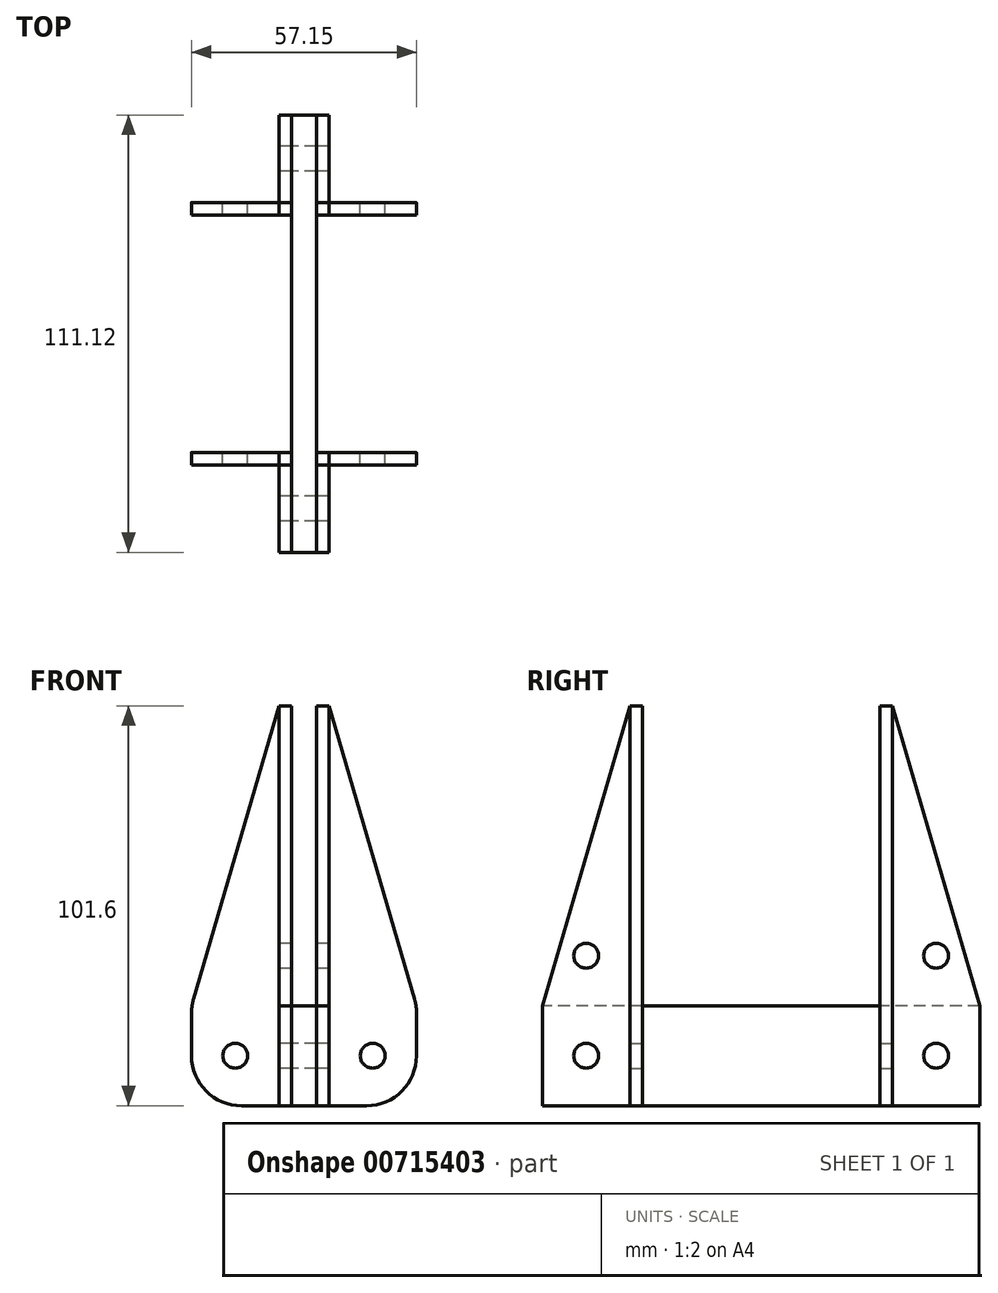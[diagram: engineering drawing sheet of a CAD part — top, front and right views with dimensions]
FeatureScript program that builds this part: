
annotation { "Feature Type Name" : "Feature", "Feature Type Description" : "" }
export const myFeature = defineFeature(function(context is Context, id is Id, definition is map)
    precondition{}
    {
        {
            var Q0;
            Q0=qCreatedBy(makeId("Top.planeOp"),FACE);
            var sketch = newSketch(context, id + "F0", { "sketchPlane" : qUnion([Q0])});
            skLineSegment(sketch, "E0.bottom", {"start": v(-15.88, 101.6) * mm, "end": v(15.87, 101.6) * mm, "construction": true});
            skLineSegment(sketch, "E0.top", {"start": v(-15.87, -101.6) * mm, "end": v(15.87, -101.6) * mm, "construction": true});
            skLineSegment(sketch, "E0.left", {"start": v(-15.88, 101.6) * mm, "end": v(-15.87, -101.6) * mm, "construction": true});
            skLineSegment(sketch, "E0.right", {"start": v(15.87, 101.6) * mm, "end": v(15.88, -101.6) * mm, "construction": true});
            skLineSegment(sketch, "E1", {"start": v(-28.57, 30.16) * mm, "end": v(-3.17, 30.16) * mm});
            skLineSegment(sketch, "E2", {"start": v(-3.17, 30.16) * mm, "end": v(-3.18, 55.56) * mm});
            skLineSegment(sketch, "E3", {"start": v(15.88, 0) * mm, "end": v(-15.87, 0) * mm, "construction": true});
            skLineSegment(sketch, "E4", {"start": v(0, 101.6) * mm, "end": v(0, -101.6) * mm, "construction": true});
            skLineSegment(sketch, "E5.0", {"start": v(-6.35, 33.34) * mm, "end": v(-6.35, 55.56) * mm});
            skLineSegment(sketch, "E5.1", {"start": v(-28.57, 33.34) * mm, "end": v(-6.35, 33.34) * mm});
            skLineSegment(sketch, "E6", {"start": v(-28.57, 33.34) * mm, "end": v(-28.57, 30.16) * mm});
            skLineSegment(sketch, "E7", {"start": v(-3.18, 55.56) * mm, "end": v(-6.35, 55.56) * mm});
            skLineSegment(sketch, "E8.MirrorCS", {"start": v(3.17, 30.16) * mm, "end": v(3.17, 55.56) * mm});
            skLineSegment(sketch, "E9.MirrorCS", {"start": v(3.17, 55.56) * mm, "end": v(6.35, 55.56) * mm});
            skLineSegment(sketch, "E10.MirrorCS", {"start": v(6.35, 33.34) * mm, "end": v(6.35, 55.56) * mm});
            skLineSegment(sketch, "E11.MirrorCS", {"start": v(28.57, 33.34) * mm, "end": v(6.35, 33.34) * mm});
            skLineSegment(sketch, "E12.MirrorCS", {"start": v(28.57, 30.16) * mm, "end": v(3.17, 30.16) * mm});
            skLineSegment(sketch, "E13.MirrorCS", {"start": v(28.58, 33.34) * mm, "end": v(28.58, 30.16) * mm});
            skLineSegment(sketch, "E14.MirrorCS", {"start": v(3.17, -55.56) * mm, "end": v(6.35, -55.56) * mm});
            skLineSegment(sketch, "E15.MirrorCS", {"start": v(-3.17, -55.56) * mm, "end": v(-6.35, -55.56) * mm});
            skLineSegment(sketch, "E16.MirrorCS", {"start": v(28.58, -33.34) * mm, "end": v(28.58, -30.16) * mm});
            skLineSegment(sketch, "E17.MirrorCS", {"start": v(-28.57, -33.34) * mm, "end": v(-28.57, -30.16) * mm});
            skLineSegment(sketch, "E18.MirrorCS", {"start": v(28.57, -33.34) * mm, "end": v(6.35, -33.34) * mm});
            skLineSegment(sketch, "E19.MirrorCS", {"start": v(28.58, -30.16) * mm, "end": v(3.17, -30.16) * mm});
            skLineSegment(sketch, "E20.MirrorCS", {"start": v(6.35, -33.34) * mm, "end": v(6.35, -55.56) * mm});
            skLineSegment(sketch, "E21.MirrorCS", {"start": v(-28.57, -30.16) * mm, "end": v(-3.17, -30.16) * mm});
            skLineSegment(sketch, "E22.MirrorCS", {"start": v(3.18, -30.16) * mm, "end": v(3.18, -55.56) * mm});
            skLineSegment(sketch, "E23.MirrorCS", {"start": v(-3.17, -30.16) * mm, "end": v(-3.17, -55.56) * mm});
            skLineSegment(sketch, "E24.MirrorCS", {"start": v(-28.57, -33.34) * mm, "end": v(-6.35, -33.34) * mm});
            skLineSegment(sketch, "E25.MirrorCS", {"start": v(-6.35, -33.34) * mm, "end": v(-6.35, -55.56) * mm});
            skLineSegment(sketch, "E26", {"start": v(-3.17, -55.56) * mm, "end": v(3.17, -55.56) * mm});
            skLineSegment(sketch, "E27", {"start": v(-3.18, 55.56) * mm, "end": v(3.17, 55.56) * mm});
            skLineSegment(sketch, "E28", {"start": v(-3.17, -30.16) * mm, "end": v(-3.18, 30.16) * mm});
            skLineSegment(sketch, "E29", {"start": v(3.17, 30.16) * mm, "end": v(3.18, -30.16) * mm});
            skSolve(sketch);
        }
        {
            var Q0;
            Q0=makeQuery(id+"F0.imprint","IMPRINT",FACE,{"disambiguationData":[TD([[makeQuery(id+"F0.imprint","IMPRINT",EDGE,{"derivedFrom":sQuery(id+"F0.wireOp",EDGE,"E1")}),1.0]])]});
            var Q1;
            Q1=makeQuery(id+"F0.imprint","IMPRINT",FACE,{"disambiguationData":[TD([[makeQuery(id+"F0.imprint","IMPRINT",EDGE,{"derivedFrom":sQuery(id+"F0.wireOp",EDGE,"E8.MirrorCS")}),-1.0]])]});
            var Q2;
            Q2=makeQuery(id+"F0.imprint","IMPRINT",FACE,{"disambiguationData":[TD([[makeQuery(id+"F0.imprint","IMPRINT",EDGE,{"derivedFrom":sQuery(id+"F0.wireOp",EDGE,"E14.MirrorCS")}),1.0]])]});
            var Q3;
            Q3=makeQuery(id+"F0.imprint","IMPRINT",FACE,{"disambiguationData":[TD([[makeQuery(id+"F0.imprint","IMPRINT",EDGE,{"derivedFrom":sQuery(id+"F0.wireOp",EDGE,"E15.MirrorCS")}),-1.0]])]});
            extrude(context, id + "F1", {"entities" : qUnion([Q0, Q1, Q2, Q3]), "depth" : 101.6 * mm, "offsetDistance" : 25.4 * mm});
        }
        {
            var Q0;
            Q0=qCreatedBy(makeId("Front.planeOp"),FACE);
            var sketch = newSketch(context, id + "F2", { "sketchPlane" : qUnion([Q0])});
            skLineSegment(sketch, "E30", {"start": v(28.07, 27.14) * mm, "end": v(6.35, 101.6) * mm});
            skLineSegment(sketch, "E31", {"start": v(6.35, 101.6) * mm, "end": v(-6.35, 101.6) * mm});
            skLineSegment(sketch, "E32", {"start": v(-6.35, 101.6) * mm, "end": v(-28.07, 27.14) * mm});
            skLineSegment(sketch, "E33", {"start": v(-28.57, 23.59) * mm, "end": v(-28.57, 12.7) * mm});
            skLineSegment(sketch, "E34", {"start": v(28.58, 23.59) * mm, "end": v(28.58, 12.7) * mm});
            skLineSegment(sketch, "E35", {"start": v(15.88, 0) * mm, "end": v(-15.87, 0) * mm});
            skCircle(sketch, "E36", {"center": v(-17.46, 12.7) * mm, "radius": 3.18 * mm});
            skPoint(sketch, "E36.centerSnap0", {"position": v(-28.57, 12.7) * mm});
            skCircle(sketch, "E37.MirrorC", {"center": v(17.46, 12.7) * mm, "radius": 3.18 * mm});
            skPoint(sketch, "E38.visualSharp", {"position": v(28.58, 0) * mm});
            skArc(sketch, "E38.filletArc", {"start": v(15.88, 0) * mm, "mid": v(24.86, 3.72) * mm, "end": v(28.58, 12.7) * mm});
            skPoint(sketch, "E39.visualSharp", {"position": v(28.58, 25.4) * mm});
            skArc(sketch, "E39.filletArc", {"start": v(28.58, 23.59) * mm, "mid": v(28.45, 25.38) * mm, "end": v(28.07, 27.14) * mm});
            skPoint(sketch, "E40.visualSharp", {"position": v(-28.57, 0) * mm});
            skArc(sketch, "E40.filletArc", {"start": v(-28.57, 12.7) * mm, "mid": v(-24.86, 3.72) * mm, "end": v(-15.87, 0) * mm});
            skPoint(sketch, "E41.visualSharp", {"position": v(-28.57, 25.4) * mm});
            skArc(sketch, "E41.filletArc", {"start": v(-28.07, 27.14) * mm, "mid": v(-28.45, 25.38) * mm, "end": v(-28.58, 23.59) * mm});
            skSolve(sketch);
        }
        {
            var Q0;
            Q0 = qSketchRegion(id + "F2", true);
            extrude(context, id + "F3", {"entities" : qUnion([Q0]), "operationType" : NewBodyOperationType.INTERSECT, "endBound" : BoundingType.SYMMETRIC, "depth" : 203.2 * mm, "offsetDistance" : 25.4 * mm});
        }
        {
            var Q0;
            Q0=makeQuery(id+"F0.imprint","IMPRINT",FACE,{"disambiguationData":[TD([[makeQuery(id+"F0.imprint","IMPRINT",EDGE,{"derivedFrom":sQuery(id+"F0.wireOp",EDGE,"E2")}),-1.0]])]});
            var Q1;
            Q1=makeQuery(id+"F0.imprint","IMPRINT",FACE,{"disambiguationData":[TD([[makeQuery(id+"F0.imprint","IMPRINT",EDGE,{"derivedFrom":sQuery(id+"F0.wireOp",EDGE,"E22.MirrorCS")}),-1.0]])]});
            extrude(context, id + "F4", {"entities" : qUnion([Q0, Q1]), "depth" : 25.4 * mm, "offsetDistance" : 25.4 * mm});
        }
        {
            var Q0;
            Q0=qCreatedBy(makeId("Right.planeOp"),FACE);
            var sketch = newSketch(context, id + "F5", { "sketchPlane" : qUnion([Q0])});
            skCircle(sketch, "E42", {"center": v(-44.45, 12.7) * mm, "radius": 3.18 * mm});
            skCircle(sketch, "E43.0.1.0", {"center": v(-44.45, 38.1) * mm, "radius": 3.18 * mm});
            skLineSegment(sketch, "E43.direction1", {"start": v(-44.45, 12.7) * mm, "end": v(6.35, 12.7) * mm, "construction": true});
            skLineSegment(sketch, "E43.direction2", {"start": v(-44.45, 12.7) * mm, "end": v(-44.45, 38.1) * mm, "construction": true});
            skCircle(sketch, "E44.MirrorC", {"center": v(44.45, 38.1) * mm, "radius": 3.18 * mm});
            skCircle(sketch, "E45.MirrorC", {"center": v(44.45, 12.7) * mm, "radius": 3.18 * mm});
            skLineSegment(sketch, "E46", {"start": v(55.56, 25.4) * mm, "end": v(33.34, 101.6) * mm});
            skLineSegment(sketch, "E47", {"start": v(33.34, 101.6) * mm, "end": v(0, 101.6) * mm});
            skLineSegment(sketch, "E48", {"start": v(33.34, 101.6) * mm, "end": v(55.56, 101.6) * mm});
            skLineSegment(sketch, "E49", {"start": v(55.56, 101.6) * mm, "end": v(55.56, 25.4) * mm});
            skLineSegment(sketch, "E50.MirrorCS", {"start": v(-55.56, 25.4) * mm, "end": v(-33.34, 101.6) * mm});
            skLineSegment(sketch, "E51.MirrorCS", {"start": v(-55.56, 101.6) * mm, "end": v(-55.56, 25.4) * mm});
            skLineSegment(sketch, "E52.MirrorCS", {"start": v(-33.34, 101.6) * mm, "end": v(-55.56, 101.6) * mm});
            skSolve(sketch);
        }
        {
            var Q0;
            Q0 = qSketchRegion(id + "F5", true);
            extrude(context, id + "F6", {"entities" : qUnion([Q0]), "operationType" : NewBodyOperationType.REMOVE, "endBound" : BoundingType.SYMMETRIC, "depth" : 101.6 * mm, "offsetDistance" : 25.4 * mm});
        }
    });
